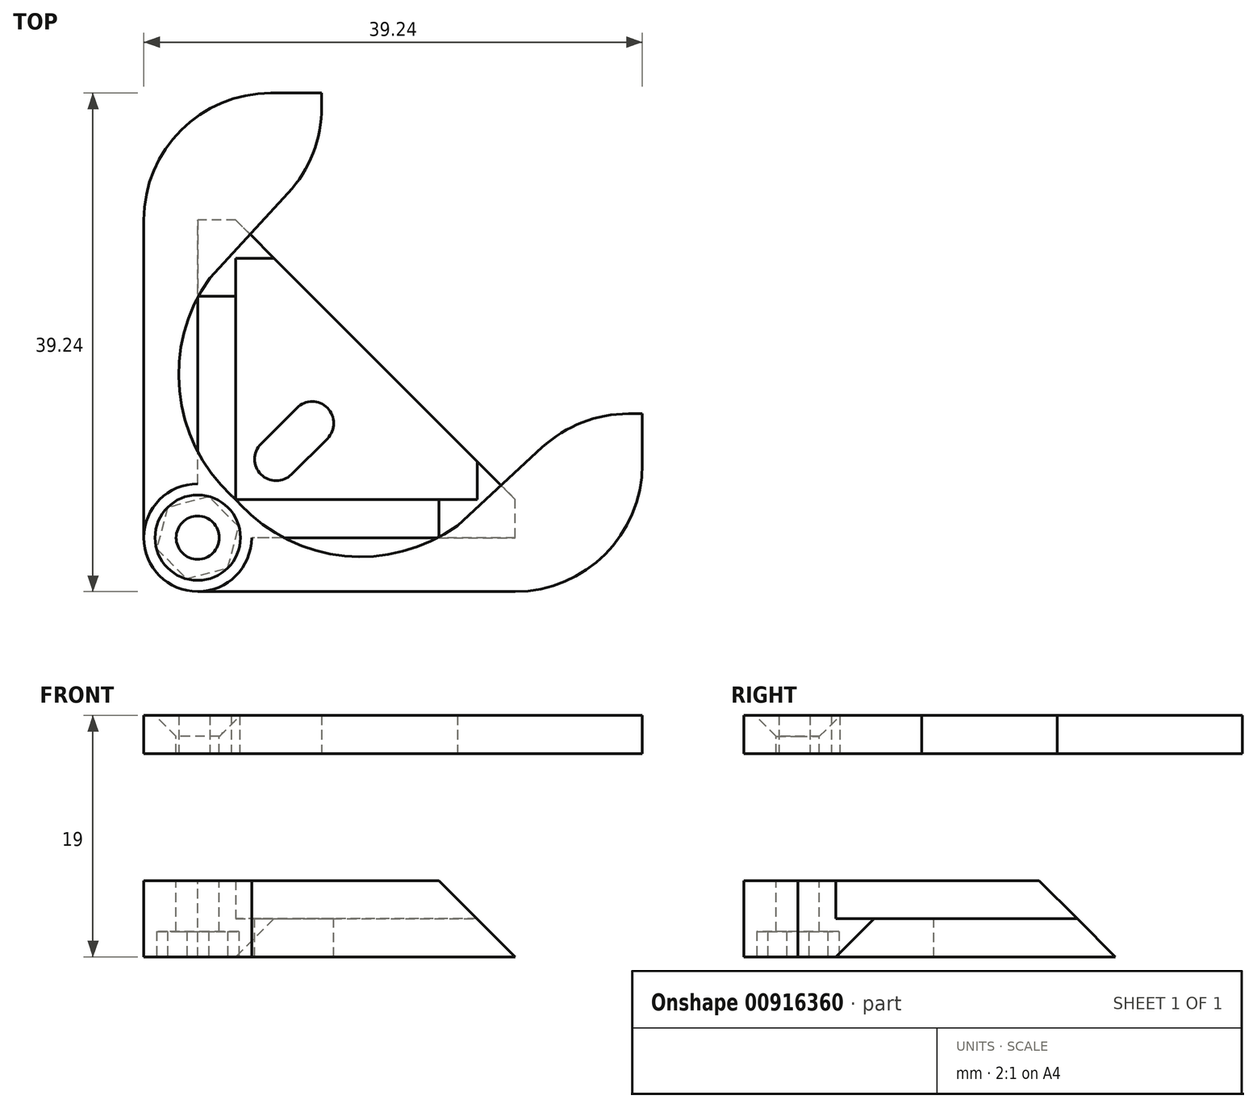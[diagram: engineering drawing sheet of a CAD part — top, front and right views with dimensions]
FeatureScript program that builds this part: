
annotation { "Feature Type Name" : "Feature", "Feature Type Description" : "" }
export const myFeature = defineFeature(function(context is Context, id is Id, definition is map)
    precondition{}
    {
        {
            var Q0;
            Q0=qCreatedBy(makeId("Top.planeOp"),FACE);
            var sketch = newSketch(context, id + "F0", { "sketchPlane" : qUnion([Q0])});
            skLineSegment(sketch, "E0.bottom", {"start": v(12.5, -12.5) * mm, "end": v(-12.5, -12.5) * mm});
            skLineSegment(sketch, "E0.top", {"start": v(12.5, 12.5) * mm, "end": v(-12.5, 12.5) * mm});
            skLineSegment(sketch, "E0.left", {"start": v(12.5, -12.5) * mm, "end": v(12.5, 12.5) * mm});
            skLineSegment(sketch, "E0.right", {"start": v(-12.5, -12.5) * mm, "end": v(-12.5, 12.5) * mm});
            skLineSegment(sketch, "E1", {"start": v(-9.5, -9.5) * mm, "end": v(-9.5, 12.5) * mm});
            skLineSegment(sketch, "E2", {"start": v(-9.5, 12.5) * mm, "end": v(12.5, -9.5) * mm});
            skLineSegment(sketch, "E3", {"start": v(12.5, -9.5) * mm, "end": v(-9.5, -9.5) * mm});
            skCircle(sketch, "E4", {"center": v(-12.5, -12.5) * mm, "radius": 4.24 * mm});
            skCircle(sketch, "E5", {"center": v(-12.5, -12.5) * mm, "radius": 1.7 * mm, "construction": true});
            skLineSegment(sketch, "E6", {"start": v(-9.5, -9.5) * mm, "end": v(-6.32, -6.32) * mm, "construction": true});
            skLineSegment(sketch, "E7", {"start": v(-6.32, -6.32) * mm, "end": v(-3.49, -3.49) * mm, "construction": true});
            skLineSegment(sketch, "E8", {"start": v(-3.49, -3.49) * mm, "end": v(0, 0) * mm, "construction": true});
            skArc(sketch, "E9.0.startCap", {"start": v(-5.12, -7.52) * mm, "mid": v(-7.52, -7.52) * mm, "end": v(-7.52, -5.12) * mm});
            skArc(sketch, "E9.0.endCap", {"start": v(-4.7, -2.29) * mm, "mid": v(-2.29, -2.29) * mm, "end": v(-2.29, -4.7) * mm});
            skLineSegment(sketch, "E9.0.left", {"start": v(-7.52, -5.12) * mm, "end": v(-4.7, -2.29) * mm});
            skLineSegment(sketch, "E9.0.right", {"start": v(-5.12, -7.52) * mm, "end": v(-2.29, -4.7) * mm});
            skSolve(sketch);
        }
        {
            var Q0;
            Q0=makeQuery(id+"F0.imprint","IMPRINT",FACE,{"disambiguationData":[TD([[makeQuery(id+"F0.imprint","IMPRINT",EDGE,{"derivedFrom":sQuery(id+"F0.wireOp",EDGE,"JHonKrWA-VV5l-fXkq-BUsN-jBxWpucY9ex3")}),-1.0]])]});
            var Q1;
            {var subQ3=sQuery(id+"F0.wireOp",EDGE,"E1");Q1=makeQuery(id+"F0.imprint","IMPRINT",FACE,{"disambiguationData":[TD([[makeQuery(id+"F0.imprint","IMPRINT",EDGE,{"derivedFrom":subQ3}),1.0]])]});}
            var Q2;
            {var subQ5=sQuery(id+"F0.wireOp",EDGE,"E3");Q2=makeQuery(id+"F0.imprint","IMPRINT",FACE,{"disambiguationData":[TD([[makeQuery(id+"F0.imprint","IMPRINT",EDGE,{"derivedFrom":subQ5}),1.0]])]});}
            var Q3;
            {var subQ0=sQuery(id+"F0.wireOp",EDGE,"E4");var subQ4=sQuery(id+"F0.wireOp",EDGE,"E0.bottom");var subQ5=makeQuery(id+"F0.imprint","INTERSECT",VERTEX,{"derivedFrom":[subQ4,subQ0]});Q3=makeQuery(id+"F0.imprint","IMPRINT",FACE,{"disambiguationData":[TD([[makeQuery(id+"F0.imprint","IMPRINT",EDGE,{"disambiguationData":[TD([[subQ5,-1.0]])],"derivedFrom":subQ4}),-1.0]])]});}
            var Q4;
            {var subQ0=sQuery(id+"F0.wireOp",EDGE,"E4");var subQ1=sQuery(id+"F0.wireOp",EDGE,"E0.bottom");var subQ2=makeQuery(id+"F0.imprint","INTERSECT",VERTEX,{"derivedFrom":[subQ1,subQ0]});Q4=makeQuery(id+"F0.imprint","IMPRINT",FACE,{"disambiguationData":[TD([[makeQuery(id+"F0.imprint","IMPRINT",EDGE,{"disambiguationData":[TD([[subQ2,-1.0]])],"derivedFrom":subQ1}),1.0]])]});}
            var Q5;
            Q5=makeQuery(id+"F0.imprint","IMPRINT",FACE,{"disambiguationData":[TD([[makeQuery(id+"F0.imprint","IMPRINT",EDGE,{"derivedFrom":sQuery(id+"F0.wireOp",EDGE,"E1")}),-1.0]])]});
            extrude(context, id + "F1", {"entities" : qUnion([Q0, Q1, Q2, Q3, Q4, Q5]), "oppositeDirection" : true, "depth" : 3 * mm, "offsetDistance" : 25 * mm});
        }
        {
            var Q0;
            {var subQ0=sQuery(id+"F0.wireOp",EDGE,"E4");var subQ1=sQuery(id+"F0.wireOp",EDGE,"E0.bottom");var subQ2=makeQuery(id+"F0.imprint","INTERSECT",VERTEX,{"derivedFrom":[subQ1,subQ0]});Q0=makeQuery(id+"F0.imprint","IMPRINT",FACE,{"disambiguationData":[TD([[makeQuery(id+"F0.imprint","IMPRINT",EDGE,{"disambiguationData":[TD([[subQ2,-1.0]])],"derivedFrom":subQ1}),1.0]])]});}
            var Q1;
            {var subQ0=sQuery(id+"F0.wireOp",EDGE,"E4");var subQ4=sQuery(id+"F0.wireOp",EDGE,"E0.bottom");var subQ5=makeQuery(id+"F0.imprint","INTERSECT",VERTEX,{"derivedFrom":[subQ4,subQ0]});Q1=makeQuery(id+"F0.imprint","IMPRINT",FACE,{"disambiguationData":[TD([[makeQuery(id+"F0.imprint","IMPRINT",EDGE,{"disambiguationData":[TD([[subQ5,-1.0]])],"derivedFrom":subQ4}),-1.0]])]});}
            var Q2;
            {var subQ3=sQuery(id+"F0.wireOp",EDGE,"E1");Q2=makeQuery(id+"F0.imprint","IMPRINT",FACE,{"disambiguationData":[TD([[makeQuery(id+"F0.imprint","IMPRINT",EDGE,{"derivedFrom":subQ3}),1.0]])]});}
            var Q3;
            {var subQ5=sQuery(id+"F0.wireOp",EDGE,"E3");Q3=makeQuery(id+"F0.imprint","IMPRINT",FACE,{"disambiguationData":[TD([[makeQuery(id+"F0.imprint","IMPRINT",EDGE,{"derivedFrom":subQ5}),1.0]])]});}
            extrude(context, id + "F2", {"entities" : qUnion([Q0, Q1, Q2, Q3]), "operationType" : NewBodyOperationType.ADD, "depth" : 3 * mm, "offsetDistance" : 25 * mm});
        }
        {
            var Q0;
            Q0=makeQuery(id+"F2.opExtrude","CAP_FACE",FACE,{"disambiguationData":[OSD([sQuery(id+"F0.wireOp",EDGE,"E0.bottom"),sQuery(id+"F0.wireOp",EDGE,"E0.top"),sQuery(id+"F0.wireOp",EDGE,"E0.left"),sQuery(id+"F0.wireOp",EDGE,"E0.right"),sQuery(id+"F0.wireOp",EDGE,"E1"),sQuery(id+"F0.wireOp",EDGE,"E3"),sQuery(id+"F0.wireOp",EDGE,"E4"),sQuery(id+"F0.wireOp",EDGE,"E5")])],"isStart":false});
            cPlane(context, id + "F3", {"entities" : qUnion([Q0]), "cplaneType" : CPlaneType.OFFSET, "offset" : 10 * mm, "width" : 150 * mm, "height" : 150 * mm});
        }
        {
            var Q0;
            Q0=qCreatedBy(id+"F3.planeOp",FACE);
            var sketch = newSketch(context, id + "F4", { "sketchPlane" : qUnion([Q0])});
            skCircle(sketch, "E10", {"center": v(-12.5, -12.5) * mm, "radius": 1.7 * mm, "construction": true});
            skCircle(sketch, "E11", {"center": v(-12.5, -12.5) * mm, "radius": 4.24 * mm});
            skLineSegment(sketch, "E12", {"start": v(-12.5, -16.74) * mm, "end": v(22.5, -16.74) * mm});
            skLineSegment(sketch, "E13", {"start": v(22.5, -16.74) * mm, "end": v(22.5, -2.74) * mm});
            skLineSegment(sketch, "E14", {"start": v(22.5, -2.74) * mm, "end": v(17.5, -2.74) * mm});
            skArc(sketch, "E15", {"start": v(-9.5, -9.5) * mm, "mid": v(-1.18, -13.91) * mm, "end": v(7.94, -11.55) * mm});
            skLineSegment(sketch, "E16", {"start": v(-16.74, -12.5) * mm, "end": v(-16.74, 22.5) * mm});
            skLineSegment(sketch, "E17", {"start": v(-16.74, 22.5) * mm, "end": v(-2.74, 22.5) * mm});
            skLineSegment(sketch, "E18", {"start": v(-2.74, 22.5) * mm, "end": v(-2.74, 17.5) * mm});
            skArc(sketch, "E19", {"start": v(-11.55, 7.94) * mm, "mid": v(-13.91, -1.18) * mm, "end": v(-9.5, -9.5) * mm});
            skLineSegment(sketch, "E20", {"start": v(-11.55, 7.94) * mm, "end": v(-2.74, 17.5) * mm});
            skLineSegment(sketch, "E21", {"start": v(7.94, -11.55) * mm, "end": v(17.5, -2.74) * mm});
            skSolve(sketch);
        }
        {
            var Q0;
            Q0 = qSketchRegion(id + "F4", true);
            extrude(context, id + "F5", {"entities" : qUnion([Q0]), "depth" : 3 * mm, "offsetDistance" : 25 * mm});
        }
        {
            var Q0;
            Q0=makeQuery(id+"F5.opExtrude","CAP_FACE",FACE,{"disambiguationData":[OSD([sQuery(id+"F4.wireOp",EDGE,"E11"),sQuery(id+"F4.wireOp",EDGE,"E12"),sQuery(id+"F4.wireOp",EDGE,"E13"),sQuery(id+"F4.wireOp",EDGE,"E14"),sQuery(id+"F4.wireOp",EDGE,"E15"),sQuery(id+"F4.wireOp",EDGE,"E16"),sQuery(id+"F4.wireOp",EDGE,"E17"),sQuery(id+"F4.wireOp",EDGE,"E18"),sQuery(id+"F4.wireOp",EDGE,"E19"),sQuery(id+"F4.wireOp",EDGE,"E20"),sQuery(id+"F4.wireOp",EDGE,"E21")])],"isStart":false});
            var sketch = newSketch(context, id + "F6", { "sketchPlane" : qUnion([Q0])});
            skPoint(sketch, "E22", {"position": v(-12.5, -12.5) * mm});
            skSolve(sketch);
        }
        {
            var Q0;
            Q0=sQuery(id+"F6.wireOp",VERTEX,"E22");
            var Q1;
            Q1=makeQuery(id+"F1.opExtrude","SWEPT_BODY",BODY,{"disambiguationData":[OSD([sQuery(id+"F0.wireOp",EDGE,"E0.bottom"),sQuery(id+"F0.wireOp",EDGE,"E0.top"),sQuery(id+"F0.wireOp",EDGE,"E0.left"),sQuery(id+"F0.wireOp",EDGE,"E0.right"),sQuery(id+"F0.wireOp",EDGE,"JHonKrWA-VV5l-fXkq-BUsN-jBxWpucY9ex3"),sQuery(id+"F0.wireOp",EDGE,"E2"),sQuery(id+"F0.wireOp",EDGE,"E4")])]});
            var Q2;
            Q2=makeQuery(id+"F5.opExtrude","SWEPT_BODY",BODY,{"disambiguationData":[OSD([sQuery(id+"F4.wireOp",EDGE,"E11"),sQuery(id+"F4.wireOp",EDGE,"E12"),sQuery(id+"F4.wireOp",EDGE,"E13"),sQuery(id+"F4.wireOp",EDGE,"E14"),sQuery(id+"F4.wireOp",EDGE,"E15"),sQuery(id+"F4.wireOp",EDGE,"E16"),sQuery(id+"F4.wireOp",EDGE,"E17"),sQuery(id+"F4.wireOp",EDGE,"E18"),sQuery(id+"F4.wireOp",EDGE,"E19"),sQuery(id+"F4.wireOp",EDGE,"E20"),sQuery(id+"F4.wireOp",EDGE,"E21")])]});
            hole(context, id + "F7", {"style" : HoleStyle.C_SINK, "endStyle" : HoleEndStyle.BLIND, "standardTappedOrClearance" : lookupTablePath({ "fit" : "Normal", "standard" : "ISO", "size" : "M3", "type" : "Clearance" }), "standardBlindInLast" : lookupTablePath({ "fit" : "Normal", "standard" : "ISO", "size" : "M3", "type" : "Clearance" }), "holeDiameter" : 3.4 * mm, "cSinkDiameter" : 6.72 * mm, "cSinkAngle" : 90 * degree, "majorDiameter" : 5 * mm, "holeDepth" : 50 * mm, "isTappedThrough" : true, "tappedDepth" : 12 * mm, "tapClearance" : 3, "locations" : qUnion([Q0]), "scope" : qUnion([Q1, Q2])});
        }
        {
            var Q0;
            Q0=makeQuery(id+"F1.opExtrude","CAP_FACE",FACE,{"disambiguationData":[OSD([sQuery(id+"F0.wireOp",EDGE,"E0.bottom"),sQuery(id+"F0.wireOp",EDGE,"E0.top"),sQuery(id+"F0.wireOp",EDGE,"E0.left"),sQuery(id+"F0.wireOp",EDGE,"E0.right"),sQuery(id+"F0.wireOp",EDGE,"JHonKrWA-VV5l-fXkq-BUsN-jBxWpucY9ex3"),sQuery(id+"F0.wireOp",EDGE,"E2"),sQuery(id+"F0.wireOp",EDGE,"E4")])],"isStart":false});
            var sketch = newSketch(context, id + "F8", { "sketchPlane" : qUnion([Q0])});
            skCircle(sketch, "E23.cCircle", {"center": v(-12.5, 12.5) * mm, "radius": 2.9 * mm, "construction": true});
            skLineSegment(sketch, "E23.0", {"start": v(-15.73, 13.37) * mm, "end": v(-13.37, 15.73) * mm});
            skLineSegment(sketch, "E23.1", {"start": v(-13.37, 15.73) * mm, "end": v(-10.13, 14.87) * mm});
            skLineSegment(sketch, "E23.2", {"start": v(-10.13, 14.87) * mm, "end": v(-9.27, 11.63) * mm});
            skLineSegment(sketch, "E23.3", {"start": v(-9.27, 11.63) * mm, "end": v(-11.63, 9.27) * mm});
            skLineSegment(sketch, "E23.4", {"start": v(-11.63, 9.27) * mm, "end": v(-14.87, 10.13) * mm});
            skLineSegment(sketch, "E23.5", {"start": v(-14.87, 10.13) * mm, "end": v(-15.73, 13.37) * mm});
            skPoint(sketch, "E23.0.midPoint", {"position": v(-14.55, 14.55) * mm});
            skLineSegment(sketch, "E24", {"start": v(-12.5, 12.5) * mm, "end": v(-17.51, 17.51) * mm, "construction": true});
            skSolve(sketch);
        }
        {
            var Q0;
            Q0 = qSketchRegion(id + "F8", true);
            extrude(context, id + "F9", {"entities" : qUnion([Q0]), "operationType" : NewBodyOperationType.REMOVE, "oppositeDirection" : true, "depth" : 2 * mm, "offsetDistance" : 25 * mm});
        }
        {
            var Q0;
            Q0=makeQuery(id+"F5.opExtrude","SWEPT_EDGE",EDGE,{"disambiguationData":[OSD([sQuery(id+"F4.wireOp",EDGE,"E16"),sQuery(id+"F4.wireOp",EDGE,"E17")])]});
            var Q1;
            Q1=makeQuery(id+"F5.opExtrude","SWEPT_EDGE",EDGE,{"disambiguationData":[OSD([sQuery(id+"F4.wireOp",EDGE,"E12"),sQuery(id+"F4.wireOp",EDGE,"E13")])]});
            var Q2;
            Q2=makeQuery(id+"F5.opExtrude","SWEPT_EDGE",EDGE,{"disambiguationData":[OSD([sQuery(id+"F4.wireOp",EDGE,"E18"),sQuery(id+"F4.wireOp",EDGE,"E20")])]});
            var Q3;
            Q3=makeQuery(id+"F5.opExtrude","SWEPT_EDGE",EDGE,{"disambiguationData":[OSD([sQuery(id+"F4.wireOp",EDGE,"E14"),sQuery(id+"F4.wireOp",EDGE,"E21")])]});
            fillet(context, id + "F10", {"entities" : qUnion([Q0, Q1, Q2, Q3]), "radius" : 10 * mm, "tangentPropagation" : true, "allowEdgeOverflow" : false});
        }
        {
            var Q0;
            Q0=makeQuery(id+"F2.opExtrude","CAP_EDGE",EDGE,{"disambiguationData":[OSD([sQuery(id+"F0.wireOp",EDGE,"E0.left")])],"isStart":false});
            var Q1;
            Q1=makeQuery(id+"F2.opExtrude","CAP_EDGE",EDGE,{"disambiguationData":[OSD([sQuery(id+"F0.wireOp",EDGE,"E0.top")])],"isStart":false});
            chamfer(context, id + "F11", {"entities" : qUnion([Q0, Q1]), "width" : 6 * mm, "tangentPropagation" : true});
        }
    });
